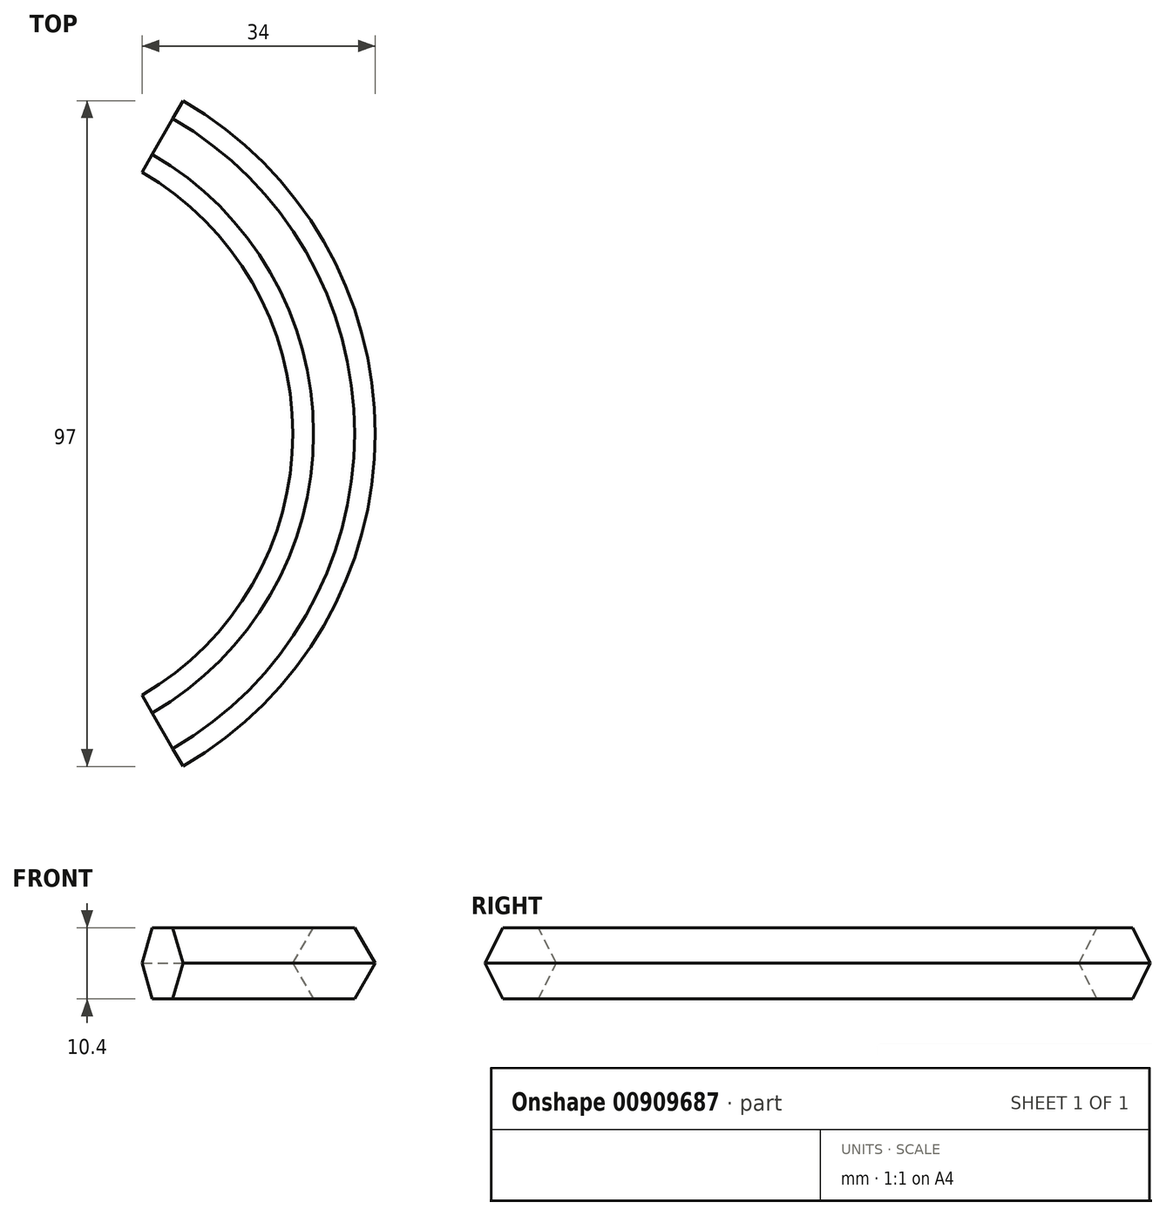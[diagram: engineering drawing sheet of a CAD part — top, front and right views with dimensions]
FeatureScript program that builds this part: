
annotation { "Feature Type Name" : "Feature", "Feature Type Description" : "" }
export const myFeature = defineFeature(function(context is Context, id is Id, definition is map)
    precondition{}
    {
        {
            var Q0;
            Q0=qCreatedBy(makeId("Front.planeOp"),FACE);
            var sketch = newSketch(context, id + "F0", { "sketchPlane" : qUnion([Q0])});
            skCircle(sketch, "E0.cCircle", {"center": v(50, 0) * mm, "radius": 6 * mm, "construction": true});
            skLineSegment(sketch, "E0.0", {"start": v(53, -5.2) * mm, "end": v(47, -5.2) * mm});
            skLineSegment(sketch, "E0.1", {"start": v(47, -5.2) * mm, "end": v(44, 0) * mm});
            skLineSegment(sketch, "E0.2", {"start": v(44, 0) * mm, "end": v(47, 5.2) * mm});
            skLineSegment(sketch, "E0.3", {"start": v(47, 5.2) * mm, "end": v(53, 5.2) * mm});
            skLineSegment(sketch, "E0.4", {"start": v(53, 5.2) * mm, "end": v(56, 0) * mm});
            skLineSegment(sketch, "E0.5", {"start": v(56, 0) * mm, "end": v(53, -5.2) * mm});
            skLineSegment(sketch, "E1", {"start": v(0, 0) * mm, "end": v(0, 20.15) * mm});
            skSolve(sketch);
        }
        {
            var Q0;
            Q0=makeQuery(id+"F0.imprint","IMPRINT",FACE,{"disambiguationData":[TD([[makeQuery(id+"F0.imprint","IMPRINT",EDGE,{"derivedFrom":sQuery(id+"F0.wireOp",EDGE,"E0.0")}),-1.0]])]});
            var Q1;
            Q1=sQuery(id+"F0.wireOp",EDGE,"E1");
            revolve(context, id + "F1", {"surfaceOperationType" : NewSurfaceOperationType.NEW, "entities" : qUnion([Q0]), "axis" : qUnion([Q1]), "revolveType" : RevolveType.SYMMETRIC, "angle" : 120 * degree});
        }
    });
